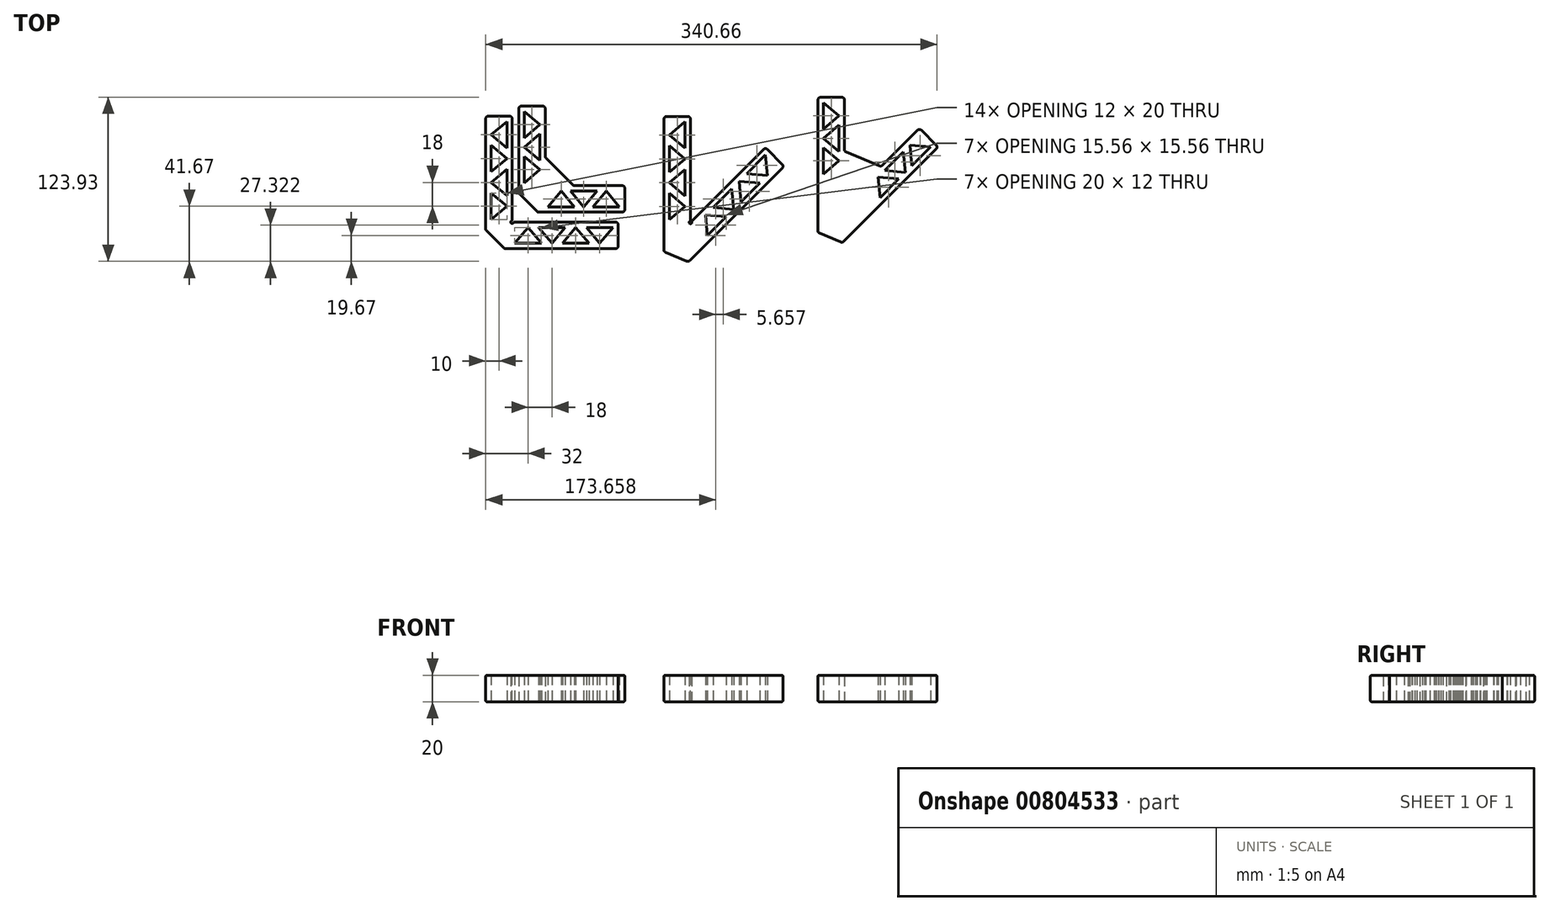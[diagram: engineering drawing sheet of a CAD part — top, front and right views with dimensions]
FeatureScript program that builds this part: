
annotation { "Feature Type Name" : "Feature", "Feature Type Description" : "" }
export const myFeature = defineFeature(function(context is Context, id is Id, definition is map)
    precondition{}
    {
        {
            var Q0;
            Q0=qCreatedBy(makeId("Top.planeOp"),FACE);
            var sketch = newSketch(context, id + "F0", { "sketchPlane" : qUnion([Q0])});
            skLineSegment(sketch, "E0", {"start": v(0, 100) * mm, "end": v(0, 14.14) * mm});
            skLineSegment(sketch, "E1", {"start": v(20, 20) * mm, "end": v(20, 100) * mm});
            skLineSegment(sketch, "E2", {"start": v(20, 100) * mm, "end": v(0, 100) * mm});
            skLineSegment(sketch, "E3", {"start": v(4, 22) * mm, "end": v(4, 42) * mm});
            skLineSegment(sketch, "E4", {"start": v(4, 42) * mm, "end": v(16, 32) * mm});
            skLineSegment(sketch, "E5", {"start": v(16, 32) * mm, "end": v(4, 22) * mm});
            skLineSegment(sketch, "E6", {"start": v(4, 58) * mm, "end": v(4, 78) * mm});
            skLineSegment(sketch, "E7", {"start": v(4, 78) * mm, "end": v(16, 68) * mm});
            skLineSegment(sketch, "E8", {"start": v(16, 68) * mm, "end": v(4, 58) * mm});
            skLineSegment(sketch, "E9", {"start": v(0, 14.14) * mm, "end": v(7.07, 7.07) * mm});
            skLineSegment(sketch, "E10", {"start": v(7.07, 7.07) * mm, "end": v(20, 20) * mm});
            skLineSegment(sketch, "E11", {"start": v(16, 96) * mm, "end": v(16, 76) * mm});
            skLineSegment(sketch, "E12", {"start": v(16, 76) * mm, "end": v(4, 86) * mm});
            skLineSegment(sketch, "E13", {"start": v(4, 86) * mm, "end": v(16, 96) * mm});
            skLineSegment(sketch, "E14", {"start": v(16, 60) * mm, "end": v(16, 40) * mm});
            skLineSegment(sketch, "E15", {"start": v(16, 40) * mm, "end": v(4, 50) * mm});
            skLineSegment(sketch, "E16", {"start": v(4, 50) * mm, "end": v(16, 60) * mm});
            skLineSegment(sketch, "E17", {"start": v(4, 86) * mm, "end": v(4, 78) * mm, "construction": true});
            skLineSegment(sketch, "E18", {"start": v(4, 58) * mm, "end": v(4, 50) * mm, "construction": true});
            skLineSegment(sketch, "E19", {"start": v(4, 50) * mm, "end": v(4, 42) * mm, "construction": true});
            skLineSegment(sketch, "E20.MirrorCS", {"start": v(40, 16) * mm, "end": v(50, 4) * mm});
            skLineSegment(sketch, "E21.MirrorCS", {"start": v(50, 4) * mm, "end": v(60, 16) * mm});
            skLineSegment(sketch, "E22.MirrorCS", {"start": v(60, 16) * mm, "end": v(40, 16) * mm});
            skLineSegment(sketch, "E23.MirrorCS", {"start": v(86, 4) * mm, "end": v(78, 4) * mm, "construction": true});
            skLineSegment(sketch, "E24.MirrorCS", {"start": v(86, 4) * mm, "end": v(96, 16) * mm});
            skLineSegment(sketch, "E25.MirrorCS", {"start": v(58, 4) * mm, "end": v(50, 4) * mm, "construction": true});
            skLineSegment(sketch, "E26.MirrorCS", {"start": v(50, 4) * mm, "end": v(42, 4) * mm, "construction": true});
            skLineSegment(sketch, "E27.MirrorCS", {"start": v(76, 16) * mm, "end": v(86, 4) * mm});
            skLineSegment(sketch, "E28.MirrorCS", {"start": v(96, 16) * mm, "end": v(76, 16) * mm});
            skLineSegment(sketch, "E29.MirrorCS", {"start": v(14.14, 0) * mm, "end": v(7.07, 7.07) * mm});
            skLineSegment(sketch, "E30.MirrorCS", {"start": v(68, 16) * mm, "end": v(58, 4) * mm});
            skLineSegment(sketch, "E31.MirrorCS", {"start": v(78, 4) * mm, "end": v(68, 16) * mm});
            skLineSegment(sketch, "E32.MirrorCS", {"start": v(58, 4) * mm, "end": v(78, 4) * mm});
            skLineSegment(sketch, "E33.MirrorCS", {"start": v(32, 16) * mm, "end": v(22, 4) * mm});
            skLineSegment(sketch, "E34.MirrorCS", {"start": v(42, 4) * mm, "end": v(32, 16) * mm});
            skLineSegment(sketch, "E35.MirrorCS", {"start": v(22, 4) * mm, "end": v(42, 4) * mm});
            skLineSegment(sketch, "E36.MirrorCS", {"start": v(100, 20) * mm, "end": v(100, 0) * mm});
            skLineSegment(sketch, "E37.MirrorCS", {"start": v(20, 20) * mm, "end": v(100, 20) * mm});
            skLineSegment(sketch, "E38.MirrorCS", {"start": v(100, 0) * mm, "end": v(14.14, 0) * mm});
            skLineSegment(sketch, "E39", {"start": v(25, 107.58) * mm, "end": v(25, 41.72) * mm});
            skLineSegment(sketch, "E40", {"start": v(45, 107.58) * mm, "end": v(25, 107.58) * mm});
            skLineSegment(sketch, "E41", {"start": v(29, 49.58) * mm, "end": v(29, 69.58) * mm});
            skLineSegment(sketch, "E42", {"start": v(29, 69.58) * mm, "end": v(41, 59.58) * mm});
            skLineSegment(sketch, "E43", {"start": v(41, 59.58) * mm, "end": v(29, 49.58) * mm});
            skLineSegment(sketch, "E44", {"start": v(29, 83.58) * mm, "end": v(29, 103.58) * mm});
            skLineSegment(sketch, "E45", {"start": v(29, 103.58) * mm, "end": v(41, 93.58) * mm});
            skLineSegment(sketch, "E46", {"start": v(41, 93.58) * mm, "end": v(29, 83.58) * mm});
            skLineSegment(sketch, "E47", {"start": v(25, 41.72) * mm, "end": v(32.08, 34.65) * mm});
            skLineSegment(sketch, "E48", {"start": v(32.08, 34.65) * mm, "end": v(55.61, 58.19) * mm});
            skLineSegment(sketch, "E49", {"start": v(41, 86.58) * mm, "end": v(41, 66.58) * mm});
            skLineSegment(sketch, "E50", {"start": v(41, 66.58) * mm, "end": v(29, 76.58) * mm});
            skLineSegment(sketch, "E51", {"start": v(29, 76.58) * mm, "end": v(41, 86.58) * mm});
            skLineSegment(sketch, "E52", {"start": v(29, 83.58) * mm, "end": v(29, 76.58) * mm, "construction": true});
            skLineSegment(sketch, "E53", {"start": v(29, 76.58) * mm, "end": v(29, 69.58) * mm, "construction": true});
            skLineSegment(sketch, "E54", {"start": v(45, 107.58) * mm, "end": v(45, 68.8) * mm});
            skLineSegment(sketch, "E55", {"start": v(45, 68.8) * mm, "end": v(55.61, 58.19) * mm});
            skLineSegment(sketch, "E56", {"start": v(45, 68.8) * mm, "end": v(45, 47.58) * mm, "construction": true});
            skLineSegment(sketch, "E57.MirrorCS", {"start": v(64, 43.58) * mm, "end": v(74, 31.58) * mm});
            skLineSegment(sketch, "E58.MirrorCS", {"start": v(47, 31.58) * mm, "end": v(67, 31.58) * mm});
            skLineSegment(sketch, "E59.MirrorCS", {"start": v(84, 43.58) * mm, "end": v(64, 43.58) * mm});
            skLineSegment(sketch, "E60.MirrorCS", {"start": v(105, 47.58) * mm, "end": v(105, 27.58) * mm});
            skLineSegment(sketch, "E61.MirrorCS", {"start": v(81, 31.58) * mm, "end": v(101, 31.58) * mm});
            skLineSegment(sketch, "E62.MirrorCS", {"start": v(105, 27.58) * mm, "end": v(39.15, 27.58) * mm});
            skLineSegment(sketch, "E63.MirrorCS", {"start": v(57, 43.58) * mm, "end": v(47, 31.58) * mm});
            skLineSegment(sketch, "E64.MirrorCS", {"start": v(105, 47.58) * mm, "end": v(66.22, 47.58) * mm});
            skLineSegment(sketch, "E65.MirrorCS", {"start": v(39.15, 27.58) * mm, "end": v(32.08, 34.65) * mm});
            skLineSegment(sketch, "E66.MirrorCS", {"start": v(74, 31.58) * mm, "end": v(67, 31.58) * mm, "construction": true});
            skLineSegment(sketch, "E67.MirrorCS", {"start": v(91, 43.58) * mm, "end": v(81, 31.58) * mm});
            skLineSegment(sketch, "E68.MirrorCS", {"start": v(66.22, 47.58) * mm, "end": v(45, 47.58) * mm, "construction": true});
            skLineSegment(sketch, "E69.MirrorCS", {"start": v(81, 31.58) * mm, "end": v(74, 31.58) * mm, "construction": true});
            skLineSegment(sketch, "E70.MirrorCS", {"start": v(101, 31.58) * mm, "end": v(91, 43.58) * mm});
            skLineSegment(sketch, "E71.MirrorCS", {"start": v(66.22, 47.58) * mm, "end": v(55.61, 58.19) * mm});
            skLineSegment(sketch, "E72.MirrorCS", {"start": v(74, 31.58) * mm, "end": v(84, 43.58) * mm});
            skLineSegment(sketch, "E73.MirrorCS", {"start": v(67, 31.58) * mm, "end": v(57, 43.58) * mm});
            skArc(sketch, "E74", {"start": v(20, 21) * mm, "mid": v(19.3, 19.3) * mm, "end": v(21, 20) * mm});
            skSolve(sketch);
        }
        {
            var Q0;
            Q0=qCreatedBy(makeId("Top.planeOp"),FACE);
            var sketch = newSketch(context, id + "F1", { "sketchPlane" : qUnion([Q0])});
            skLineSegment(sketch, "E75", {"start": v(134.57, 99.77) * mm, "end": v(134.57, -2.38) * mm});
            skLineSegment(sketch, "E76", {"start": v(154.57, 19.77) * mm, "end": v(154.57, 99.77) * mm});
            skLineSegment(sketch, "E77", {"start": v(154.57, 99.77) * mm, "end": v(134.57, 99.77) * mm});
            skLineSegment(sketch, "E78", {"start": v(138.57, 21.77) * mm, "end": v(138.57, 41.77) * mm});
            skLineSegment(sketch, "E79", {"start": v(138.57, 41.77) * mm, "end": v(150.57, 31.77) * mm});
            skLineSegment(sketch, "E80", {"start": v(150.57, 31.77) * mm, "end": v(138.57, 21.77) * mm});
            skLineSegment(sketch, "E81", {"start": v(138.57, 57.77) * mm, "end": v(138.57, 77.77) * mm});
            skLineSegment(sketch, "E82", {"start": v(138.57, 77.77) * mm, "end": v(150.57, 67.77) * mm});
            skLineSegment(sketch, "E83", {"start": v(150.57, 67.77) * mm, "end": v(138.57, 57.77) * mm});
            skLineSegment(sketch, "E84", {"start": v(134.57, -2.38) * mm, "end": v(143.8, -6.2) * mm});
            skLineSegment(sketch, "E85", {"start": v(143.8, -6.2) * mm, "end": v(154.57, 19.77) * mm});
            skLineSegment(sketch, "E86", {"start": v(150.57, 95.77) * mm, "end": v(150.57, 75.77) * mm});
            skLineSegment(sketch, "E87", {"start": v(150.57, 75.77) * mm, "end": v(138.57, 85.77) * mm});
            skLineSegment(sketch, "E88", {"start": v(138.57, 85.77) * mm, "end": v(150.57, 95.77) * mm});
            skLineSegment(sketch, "E89", {"start": v(150.57, 59.77) * mm, "end": v(150.57, 39.77) * mm});
            skLineSegment(sketch, "E90", {"start": v(150.57, 39.77) * mm, "end": v(138.57, 49.77) * mm});
            skLineSegment(sketch, "E91", {"start": v(138.57, 49.77) * mm, "end": v(150.57, 59.77) * mm});
            skLineSegment(sketch, "E92", {"start": v(138.57, 85.77) * mm, "end": v(138.57, 77.77) * mm, "construction": true});
            skLineSegment(sketch, "E93", {"start": v(138.57, 57.77) * mm, "end": v(138.57, 49.77) * mm, "construction": true});
            skLineSegment(sketch, "E94", {"start": v(138.57, 49.77) * mm, "end": v(138.57, 41.77) * mm, "construction": true});
            skLineSegment(sketch, "E95.MirrorCS", {"start": v(171.54, 31.09) * mm, "end": v(187.1, 29.67) * mm});
            skLineSegment(sketch, "E96.MirrorCS", {"start": v(187.1, 29.67) * mm, "end": v(185.68, 45.23) * mm});
            skLineSegment(sketch, "E97.MirrorCS", {"start": v(185.68, 45.23) * mm, "end": v(171.54, 31.09) * mm});
            skLineSegment(sketch, "E98.MirrorCS", {"start": v(212.55, 55.13) * mm, "end": v(206.9, 49.47) * mm, "construction": true});
            skLineSegment(sketch, "E99.MirrorCS", {"start": v(212.55, 55.13) * mm, "end": v(211.13, 70.68) * mm});
            skLineSegment(sketch, "E100.MirrorCS", {"start": v(192.75, 35.33) * mm, "end": v(187.1, 29.67) * mm, "construction": true});
            skLineSegment(sketch, "E101.MirrorCS", {"start": v(187.1, 29.67) * mm, "end": v(181.44, 24.02) * mm, "construction": true});
            skLineSegment(sketch, "E102.MirrorCS", {"start": v(197, 56.54) * mm, "end": v(212.55, 55.13) * mm});
            skLineSegment(sketch, "E103.MirrorCS", {"start": v(211.13, 70.68) * mm, "end": v(197, 56.54) * mm});
            skLineSegment(sketch, "E104.MirrorCS", {"start": v(153.04, -10.03) * mm, "end": v(143.8, -6.2) * mm});
            skLineSegment(sketch, "E105.MirrorCS", {"start": v(191.34, 50.89) * mm, "end": v(192.75, 35.33) * mm});
            skLineSegment(sketch, "E106.MirrorCS", {"start": v(206.9, 49.47) * mm, "end": v(191.34, 50.89) * mm});
            skLineSegment(sketch, "E107.MirrorCS", {"start": v(192.75, 35.33) * mm, "end": v(206.9, 49.47) * mm});
            skLineSegment(sketch, "E108.MirrorCS", {"start": v(165.88, 25.43) * mm, "end": v(167.3, 9.87) * mm});
            skLineSegment(sketch, "E109.MirrorCS", {"start": v(181.44, 24.02) * mm, "end": v(165.88, 25.43) * mm});
            skLineSegment(sketch, "E110.MirrorCS", {"start": v(167.3, 9.87) * mm, "end": v(181.44, 24.02) * mm});
            skLineSegment(sketch, "E111.MirrorCS", {"start": v(211.13, 76.34) * mm, "end": v(225.28, 62.2) * mm});
            skLineSegment(sketch, "E112.MirrorCS", {"start": v(154.57, 19.77) * mm, "end": v(211.13, 76.34) * mm});
            skLineSegment(sketch, "E113.MirrorCS", {"start": v(225.28, 62.2) * mm, "end": v(153.04, -10.03) * mm});
            skLineSegment(sketch, "E114", {"start": v(250.78, 114.26) * mm, "end": v(250.78, 12.1) * mm});
            skLineSegment(sketch, "E115", {"start": v(270.78, 114.26) * mm, "end": v(250.78, 114.26) * mm});
            skLineSegment(sketch, "E116", {"start": v(254.78, 56.26) * mm, "end": v(254.78, 76.26) * mm});
            skLineSegment(sketch, "E117", {"start": v(254.78, 76.26) * mm, "end": v(266.78, 66.26) * mm});
            skLineSegment(sketch, "E118", {"start": v(266.78, 66.26) * mm, "end": v(254.78, 56.26) * mm});
            skLineSegment(sketch, "E119", {"start": v(254.78, 90.26) * mm, "end": v(254.78, 110.26) * mm});
            skLineSegment(sketch, "E120", {"start": v(254.78, 110.26) * mm, "end": v(266.78, 100.26) * mm});
            skLineSegment(sketch, "E121", {"start": v(266.78, 100.26) * mm, "end": v(254.78, 90.26) * mm});
            skLineSegment(sketch, "E122", {"start": v(250.78, 12.1) * mm, "end": v(260.02, 8.28) * mm});
            skLineSegment(sketch, "E123", {"start": v(260.02, 8.28) * mm, "end": v(284.64, 67.71) * mm});
            skLineSegment(sketch, "E124", {"start": v(266.78, 93.26) * mm, "end": v(266.78, 73.26) * mm});
            skLineSegment(sketch, "E125", {"start": v(266.78, 73.26) * mm, "end": v(254.78, 83.26) * mm});
            skLineSegment(sketch, "E126", {"start": v(254.78, 83.26) * mm, "end": v(266.78, 93.26) * mm});
            skLineSegment(sketch, "E127", {"start": v(254.78, 90.26) * mm, "end": v(254.78, 83.26) * mm, "construction": true});
            skLineSegment(sketch, "E128", {"start": v(254.78, 83.26) * mm, "end": v(254.78, 76.26) * mm, "construction": true});
            skLineSegment(sketch, "E129", {"start": v(270.78, 114.26) * mm, "end": v(270.78, 73.45) * mm});
            skLineSegment(sketch, "E130", {"start": v(270.78, 73.45) * mm, "end": v(284.64, 67.71) * mm});
            skLineSegment(sketch, "E131", {"start": v(270.78, 73.45) * mm, "end": v(270.78, 34.26) * mm, "construction": true});
            skLineSegment(sketch, "E132.MirrorCS", {"start": v(301.19, 59) * mm, "end": v(316.74, 57.59) * mm});
            skLineSegment(sketch, "E133.MirrorCS", {"start": v(297.65, 38.5) * mm, "end": v(311.8, 52.64) * mm});
            skLineSegment(sketch, "E134.MirrorCS", {"start": v(315.33, 73.15) * mm, "end": v(301.19, 59) * mm});
            skLineSegment(sketch, "E135.MirrorCS", {"start": v(327.35, 90.82) * mm, "end": v(341.5, 76.68) * mm});
            skLineSegment(sketch, "E136.MirrorCS", {"start": v(321.7, 62.54) * mm, "end": v(335.83, 76.68) * mm});
            skLineSegment(sketch, "E137.MirrorCS", {"start": v(341.5, 76.68) * mm, "end": v(269.26, 4.45) * mm});
            skLineSegment(sketch, "E138.MirrorCS", {"start": v(296.24, 54.05) * mm, "end": v(297.65, 38.5) * mm});
            skLineSegment(sketch, "E139.MirrorCS", {"start": v(327.35, 90.82) * mm, "end": v(298.5, 61.97) * mm});
            skLineSegment(sketch, "E140.MirrorCS", {"start": v(269.26, 4.45) * mm, "end": v(260.02, 8.28) * mm});
            skLineSegment(sketch, "E141.MirrorCS", {"start": v(316.74, 57.59) * mm, "end": v(311.8, 52.64) * mm, "construction": true});
            skLineSegment(sketch, "E142.MirrorCS", {"start": v(320.28, 78.1) * mm, "end": v(321.7, 62.54) * mm});
            skLineSegment(sketch, "E143.MirrorCS", {"start": v(298.5, 61.97) * mm, "end": v(270.78, 34.26) * mm, "construction": true});
            skLineSegment(sketch, "E144.MirrorCS", {"start": v(321.7, 62.54) * mm, "end": v(316.74, 57.59) * mm, "construction": true});
            skLineSegment(sketch, "E145.MirrorCS", {"start": v(335.83, 76.68) * mm, "end": v(320.28, 78.1) * mm});
            skLineSegment(sketch, "E146.MirrorCS", {"start": v(298.5, 61.97) * mm, "end": v(284.64, 67.71) * mm});
            skLineSegment(sketch, "E147.MirrorCS", {"start": v(316.74, 57.59) * mm, "end": v(315.33, 73.15) * mm});
            skLineSegment(sketch, "E148.MirrorCS", {"start": v(311.8, 52.64) * mm, "end": v(296.24, 54.05) * mm});
            skArc(sketch, "E149", {"start": v(154.57, 20.77) * mm, "mid": v(154.18, 18.85) * mm, "end": v(155.27, 20.48) * mm});
            skSolve(sketch);
        }
        {
            var Q0;
            Q0=makeQuery(id+"F0.imprint","IMPRINT",FACE,{"disambiguationData":[TD([[makeQuery(id+"F0.imprint","IMPRINT",EDGE,{"derivedFrom":sQuery(id+"F0.wireOp",EDGE,"E0")}),1.0]])]});
            var Q1;
            Q1=makeQuery(id+"F0.imprint","IMPRINT",FACE,{"disambiguationData":[TD([[makeQuery(id+"F0.imprint","IMPRINT",EDGE,{"derivedFrom":sQuery(id+"F0.wireOp",EDGE,"E39")}),1.0]])]});
            var Q2;
            Q2=makeQuery(id+"F0.imprint","IMPRINT",FACE,{"disambiguationData":[TD([[makeQuery(id+"F0.imprint","IMPRINT",EDGE,{"derivedFrom":sQuery(id+"F0.wireOp",EDGE,"E48")}),-1.0]])]});
            var Q3;
            Q3=makeQuery(id+"F0.imprint","IMPRINT",FACE,{"disambiguationData":[TD([[makeQuery(id+"F0.imprint","IMPRINT",EDGE,{"derivedFrom":sQuery(id+"F0.wireOp",EDGE,"E20.MirrorCS")}),-1.0]])]});
            var Q4;
            Q4=makeQuery(id+"F1.imprint","IMPRINT",FACE,{"disambiguationData":[TD([[makeQuery(id+"F1.imprint","IMPRINT",EDGE,{"derivedFrom":sQuery(id+"F1.wireOp",EDGE,"E75")}),1.0]])]});
            var Q5;
            Q5=makeQuery(id+"F1.imprint","IMPRINT",FACE,{"disambiguationData":[TD([[makeQuery(id+"F1.imprint","IMPRINT",EDGE,{"derivedFrom":sQuery(id+"F1.wireOp",EDGE,"E95.MirrorCS")}),-1.0]])]});
            var Q6;
            Q6=makeQuery(id+"F1.imprint","IMPRINT",FACE,{"disambiguationData":[TD([[makeQuery(id+"F1.imprint","IMPRINT",EDGE,{"derivedFrom":sQuery(id+"F1.wireOp",EDGE,"E114")}),1.0]])]});
            var Q7;
            Q7=makeQuery(id+"F1.imprint","IMPRINT",FACE,{"disambiguationData":[TD([[makeQuery(id+"F1.imprint","IMPRINT",EDGE,{"derivedFrom":sQuery(id+"F1.wireOp",EDGE,"E123")}),-1.0]])]});
            extrude(context, id + "F2", {"entities" : qUnion([Q0, Q1, Q2, Q3, Q4, Q5, Q6, Q7]), "depth" : 20 * mm, "offsetDistance" : 25 * mm});
        }
        {
            var Q0;
            Q0=makeQuery(id+"F2.opExtrude","SWEPT_EDGE",EDGE,{"disambiguationData":[OSD([sQuery(id+"F0.wireOp",EDGE,"E60.MirrorCS"),sQuery(id+"F0.wireOp",EDGE,"E64.MirrorCS")])]});
            var Q1;
            Q1=makeQuery(id+"F2.opExtrude","SWEPT_EDGE",EDGE,{"disambiguationData":[OSD([sQuery(id+"F0.wireOp",EDGE,"E60.MirrorCS"),sQuery(id+"F0.wireOp",EDGE,"E62.MirrorCS")])]});
            var Q2;
            Q2=makeQuery(id+"F2.opExtrude","SWEPT_EDGE",EDGE,{"disambiguationData":[OSD([sQuery(id+"F0.wireOp",EDGE,"E36.MirrorCS"),sQuery(id+"F0.wireOp",EDGE,"E37.MirrorCS")])]});
            var Q3;
            Q3=makeQuery(id+"F2.opExtrude","SWEPT_EDGE",EDGE,{"disambiguationData":[OSD([sQuery(id+"F0.wireOp",EDGE,"E36.MirrorCS"),sQuery(id+"F0.wireOp",EDGE,"E38.MirrorCS")])]});
            var Q4;
            Q4=makeQuery(id+"F2.opExtrude","SWEPT_EDGE",EDGE,{"disambiguationData":[OSD([sQuery(id+"F0.wireOp",EDGE,"E62.MirrorCS"),sQuery(id+"F0.wireOp",EDGE,"E65.MirrorCS")])]});
            var Q5;
            Q5=makeQuery(id+"F2.opExtrude","SWEPT_EDGE",EDGE,{"disambiguationData":[OSD([sQuery(id+"F0.wireOp",EDGE,"E64.MirrorCS"),sQuery(id+"F0.wireOp",EDGE,"E71.MirrorCS")])]});
            var Q6;
            Q6=makeQuery(id+"F2.opExtrude","SWEPT_EDGE",EDGE,{"disambiguationData":[OSD([sQuery(id+"F0.wireOp",EDGE,"E54"),sQuery(id+"F0.wireOp",EDGE,"E55")])]});
            var Q7;
            Q7=makeQuery(id+"F2.opExtrude","SWEPT_EDGE",EDGE,{"disambiguationData":[OSD([sQuery(id+"F0.wireOp",EDGE,"E40"),sQuery(id+"F0.wireOp",EDGE,"E54")])]});
            var Q8;
            Q8=makeQuery(id+"F2.opExtrude","SWEPT_EDGE",EDGE,{"disambiguationData":[OSD([sQuery(id+"F0.wireOp",EDGE,"E39"),sQuery(id+"F0.wireOp",EDGE,"E40")])]});
            var Q9;
            Q9=makeQuery(id+"F2.opExtrude","SWEPT_EDGE",EDGE,{"disambiguationData":[OSD([sQuery(id+"F0.wireOp",EDGE,"E39"),sQuery(id+"F0.wireOp",EDGE,"E47")])]});
            var Q10;
            Q10=makeQuery(id+"F2.opExtrude","SWEPT_EDGE",EDGE,{"disambiguationData":[OSD([sQuery(id+"F0.wireOp",EDGE,"E0"),sQuery(id+"F0.wireOp",EDGE,"E9")])]});
            var Q11;
            Q11=makeQuery(id+"F2.opExtrude","SWEPT_EDGE",EDGE,{"disambiguationData":[OSD([sQuery(id+"F0.wireOp",EDGE,"E29.MirrorCS"),sQuery(id+"F0.wireOp",EDGE,"E38.MirrorCS")])]});
            var Q12;
            Q12=makeQuery(id+"F2.opExtrude","SWEPT_EDGE",EDGE,{"disambiguationData":[OSD([sQuery(id+"F0.wireOp",EDGE,"E0"),sQuery(id+"F0.wireOp",EDGE,"E2")])]});
            var Q13;
            Q13=makeQuery(id+"F2.opExtrude","SWEPT_EDGE",EDGE,{"disambiguationData":[OSD([sQuery(id+"F0.wireOp",EDGE,"E1"),sQuery(id+"F0.wireOp",EDGE,"E2")])]});
            var Q14;
            Q14=makeQuery(id+"F2.opExtrude","SWEPT_EDGE",EDGE,{"disambiguationData":[OSD([sQuery(id+"F0.wireOp",EDGE,"E1"),sQuery(id+"F0.wireOp",EDGE,"E74")])]});
            var Q15;
            Q15=makeQuery(id+"F2.opExtrude","SWEPT_EDGE",EDGE,{"disambiguationData":[OSD([sQuery(id+"F0.wireOp",EDGE,"E37.MirrorCS"),sQuery(id+"F0.wireOp",EDGE,"E74")])]});
            var Q16;
            Q16=makeQuery(id+"F2.opExtrude","SWEPT_EDGE",EDGE,{"disambiguationData":[OSD([sQuery(id+"F1.wireOp",EDGE,"E104.MirrorCS"),sQuery(id+"F1.wireOp",EDGE,"E113.MirrorCS")])]});
            var Q17;
            Q17=makeQuery(id+"F2.opExtrude","SWEPT_EDGE",EDGE,{"disambiguationData":[OSD([sQuery(id+"F1.wireOp",EDGE,"E75"),sQuery(id+"F1.wireOp",EDGE,"E84")])]});
            var Q18;
            Q18=makeQuery(id+"F2.opExtrude","SWEPT_EDGE",EDGE,{"disambiguationData":[OSD([sQuery(id+"F1.wireOp",EDGE,"E137.MirrorCS"),sQuery(id+"F1.wireOp",EDGE,"E140.MirrorCS")])]});
            var Q19;
            Q19=makeQuery(id+"F2.opExtrude","SWEPT_EDGE",EDGE,{"disambiguationData":[OSD([sQuery(id+"F1.wireOp",EDGE,"E114"),sQuery(id+"F1.wireOp",EDGE,"E122")])]});
            var Q20;
            Q20=makeQuery(id+"F2.opExtrude","SWEPT_EDGE",EDGE,{"disambiguationData":[OSD([sQuery(id+"F1.wireOp",EDGE,"E135.MirrorCS"),sQuery(id+"F1.wireOp",EDGE,"E137.MirrorCS")])]});
            var Q21;
            Q21=makeQuery(id+"F2.opExtrude","SWEPT_EDGE",EDGE,{"disambiguationData":[OSD([sQuery(id+"F1.wireOp",EDGE,"E135.MirrorCS"),sQuery(id+"F1.wireOp",EDGE,"E139.MirrorCS")])]});
            var Q22;
            Q22=makeQuery(id+"F2.opExtrude","SWEPT_EDGE",EDGE,{"disambiguationData":[OSD([sQuery(id+"F1.wireOp",EDGE,"E129"),sQuery(id+"F1.wireOp",EDGE,"E130")])]});
            var Q23;
            Q23=makeQuery(id+"F2.opExtrude","SWEPT_EDGE",EDGE,{"disambiguationData":[OSD([sQuery(id+"F1.wireOp",EDGE,"E115"),sQuery(id+"F1.wireOp",EDGE,"E129")])]});
            var Q24;
            Q24=makeQuery(id+"F2.opExtrude","SWEPT_EDGE",EDGE,{"disambiguationData":[OSD([sQuery(id+"F1.wireOp",EDGE,"E114"),sQuery(id+"F1.wireOp",EDGE,"E115")])]});
            var Q25;
            Q25=makeQuery(id+"F2.opExtrude","SWEPT_EDGE",EDGE,{"disambiguationData":[OSD([sQuery(id+"F1.wireOp",EDGE,"E139.MirrorCS"),sQuery(id+"F1.wireOp",EDGE,"E146.MirrorCS")])]});
            var Q26;
            Q26=makeQuery(id+"F2.opExtrude","SWEPT_EDGE",EDGE,{"disambiguationData":[OSD([sQuery(id+"F1.wireOp",EDGE,"E111.MirrorCS"),sQuery(id+"F1.wireOp",EDGE,"E113.MirrorCS")])]});
            var Q27;
            Q27=makeQuery(id+"F2.opExtrude","SWEPT_EDGE",EDGE,{"disambiguationData":[OSD([sQuery(id+"F1.wireOp",EDGE,"E111.MirrorCS"),sQuery(id+"F1.wireOp",EDGE,"E112.MirrorCS")])]});
            var Q28;
            Q28=makeQuery(id+"F2.opExtrude","SWEPT_EDGE",EDGE,{"disambiguationData":[OSD([sQuery(id+"F1.wireOp",EDGE,"E76"),sQuery(id+"F1.wireOp",EDGE,"E77")])]});
            var Q29;
            Q29=makeQuery(id+"F2.opExtrude","SWEPT_EDGE",EDGE,{"disambiguationData":[OSD([sQuery(id+"F1.wireOp",EDGE,"E75"),sQuery(id+"F1.wireOp",EDGE,"E77")])]});
            var Q30;
            Q30=makeQuery(id+"F2.opExtrude","SWEPT_EDGE",EDGE,{"disambiguationData":[OSD([sQuery(id+"F1.wireOp",EDGE,"E112.MirrorCS"),sQuery(id+"F1.wireOp",EDGE,"E149")])]});
            var Q31;
            Q31=makeQuery(id+"F2.opExtrude","SWEPT_EDGE",EDGE,{"disambiguationData":[OSD([sQuery(id+"F1.wireOp",EDGE,"E76"),sQuery(id+"F1.wireOp",EDGE,"E149")])]});
            fillet(context, id + "F3", {"entities" : qUnion([Q0, Q1, Q2, Q3, Q4, Q5, Q6, Q7, Q8, Q9, Q10, Q11, Q12, Q13, Q14, Q15, Q16, Q17, Q18, Q19, Q20, Q21, Q22, Q23, Q24, Q25, Q26, Q27, Q28, Q29, Q30, Q31]), "radius" : 2 * mm, "tangentPropagation" : true, "allowEdgeOverflow" : false});
        }
        {
            var Q0;
            Q0=makeQuery(id+"F2.opExtrude","CAP_EDGE",EDGE,{"disambiguationData":[OSD([sQuery(id+"F0.wireOp",EDGE,"E0")])],"isStart":false});
            var Q1;
            Q1=makeQuery(id+"F2.opExtrude","CAP_EDGE",EDGE,{"disambiguationData":[OSD([sQuery(id+"F0.wireOp",EDGE,"E47"),sQuery(id+"F0.wireOp",EDGE,"E65.MirrorCS")])],"isStart":false});
            var Q2;
            Q2=makeQuery(id+"F2.opExtrude","CAP_EDGE",EDGE,{"disambiguationData":[OSD([sQuery(id+"F0.wireOp",EDGE,"E37.MirrorCS")])],"isStart":true});
            var Q3;
            Q3=makeQuery(id+"F2.opExtrude","CAP_EDGE",EDGE,{"disambiguationData":[OSD([sQuery(id+"F0.wireOp",EDGE,"E62.MirrorCS")])],"isStart":true});
            var Q4;
            Q4=makeQuery(id+"F2.opExtrude","CAP_EDGE",EDGE,{"disambiguationData":[OSD([sQuery(id+"F1.wireOp",EDGE,"E76")])],"isStart":false});
            var Q5;
            Q5=makeQuery(id+"F2.opExtrude","CAP_EDGE",EDGE,{"disambiguationData":[OSD([sQuery(id+"F1.wireOp",EDGE,"E76")])],"isStart":true});
            var Q6;
            Q6=makeQuery(id+"F2.opExtrude","CAP_EDGE",EDGE,{"disambiguationData":[OSD([sQuery(id+"F1.wireOp",EDGE,"E130"),sQuery(id+"F1.wireOp",EDGE,"E146.MirrorCS")])],"isStart":false});
            var Q7;
            Q7=makeQuery(id+"F2.opExtrude","CAP_EDGE",EDGE,{"disambiguationData":[OSD([sQuery(id+"F1.wireOp",EDGE,"E130"),sQuery(id+"F1.wireOp",EDGE,"E146.MirrorCS")])],"isStart":true});
            fillet(context, id + "F4", {"entities" : qUnion([Q0, Q1, Q2, Q3, Q4, Q5, Q6, Q7]), "radius" : 1 * mm, "tangentPropagation" : true, "allowEdgeOverflow" : false});
        }
    });
